# Revit family: Faucet-Two_Handle-American_Standard-Monterrey-65001X5_Series
name_source: partatom
category: Plumbing Fixtures
revit_build: Autodesk Revit 2018 (Build: 20170223_1515(x64)
units: mm (PartAtom-declared; Revit-internal decimal feet)

## family parameters
Always vertical = No
Cut with Voids When Loaded = No
OmniClass Number = 23.45.55.17
OmniClass Title = Mixing Faucets
Part Type = Normal
Room Calculation Point = No
Round Connector Dimension = Use Diameter
Shared = Yes
Work Plane-Based = Yes

## types (2) — shared parameters
ADA Compliant = Yes
Assembly Code = D2020300
CEC Compliant = Yes
CW Connection = Yes
CWFU = 1.5
CalGreen Compliant = Yes
Cold Water Connection Diameter = 1/2"
Compliance Certifications = These products meet or exceed the following codes and standards: ANSI 117.1, ASME A112.18.1,CSA B125.1,NSF 372
Default Elevation = 0"
Finish = Brass-American Standard-002-Polished Chrome
Flow Rate = 0.5 gpm (1.9 Lpm)
HW Connection = Yes
HWFU = 1.5
Height = 3 1/4"
Hot Water Connection Diameter = 1/2"
Installation Type = Deck Mounted
Length = 4 1/16"
Manufacturer = American Standard
Material = Brass-American Standard-002-Polished Chrome
Product Documentation Link = https://americanstandard.box.com
Product Page URL = https://www.americanstandard-us.com
Revised Date = 08/14/2022
URL = http://www.americanstandard-us.com
Vent Connection = No
Waste Connection = No
Width = 15 3/4"
zero-valued in all types: WFU

## per-type parameters (varying)
| type | Description | Lever Handles | Wrist Blade Handles |
| 6500145.002 | Monterrey® 8-Inch Widespread Cast Faucet With Lever Handles 0.5 gpm/1.9 Lpm | Yes | No |
| 6500175.002 | Monterrey® 8-Inch Widespread Cast Faucet With Wrist Blade Handles 0.5 gpm/1.9 Lpm | No | Yes |

note: column(s) folded — value = type name in every type: Model

## geometry (parser evidence)
native form markers: Sweep x2
no freeform markers — native parametric forms only
